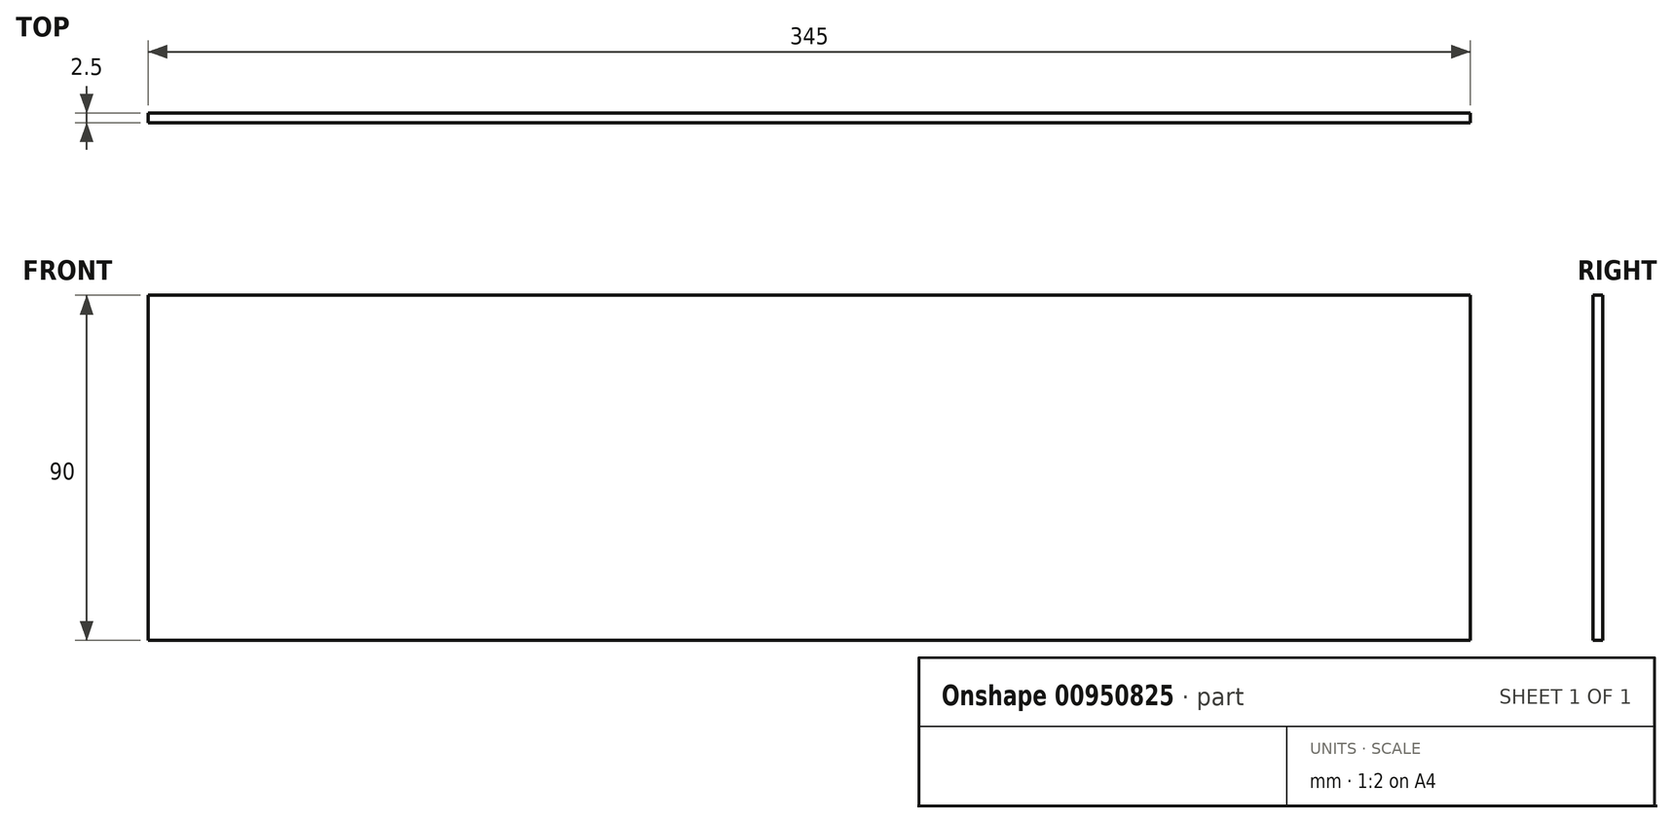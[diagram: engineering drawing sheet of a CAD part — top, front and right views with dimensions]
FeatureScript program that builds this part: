
annotation { "Feature Type Name" : "Feature", "Feature Type Description" : "" }
export const myFeature = defineFeature(function(context is Context, id is Id, definition is map)
    precondition{}
    {
        {
            var Q0;
            Q0=qCreatedBy(makeId("Front.planeOp"),FACE);
            var sketch = newSketch(context, id + "F0", { "sketchPlane" : qUnion([Q0])});
            skLineSegment(sketch, "E0.bottom", {"start": v(172.5, 45) * mm, "end": v(-172.5, 45) * mm});
            skLineSegment(sketch, "E0.top", {"start": v(172.5, -45) * mm, "end": v(-172.5, -45) * mm});
            skLineSegment(sketch, "E0.left", {"start": v(172.5, 45) * mm, "end": v(172.5, -45) * mm});
            skLineSegment(sketch, "E0.right", {"start": v(-172.5, 45) * mm, "end": v(-172.5, -45) * mm});
            skPoint(sketch, "E0.middle", {"position": v(0, 0) * mm});
            skSolve(sketch);
        }
        {
            var Q0;
            Q0=qSketchRegion(id+"F0",true);
            extrude(context, id + "F1", {"entities" : qUnion([Q0]), "oppositeDirection" : true, "depth" : 2.5 * mm, "offsetDistance" : 25 * mm});
        }
    });
